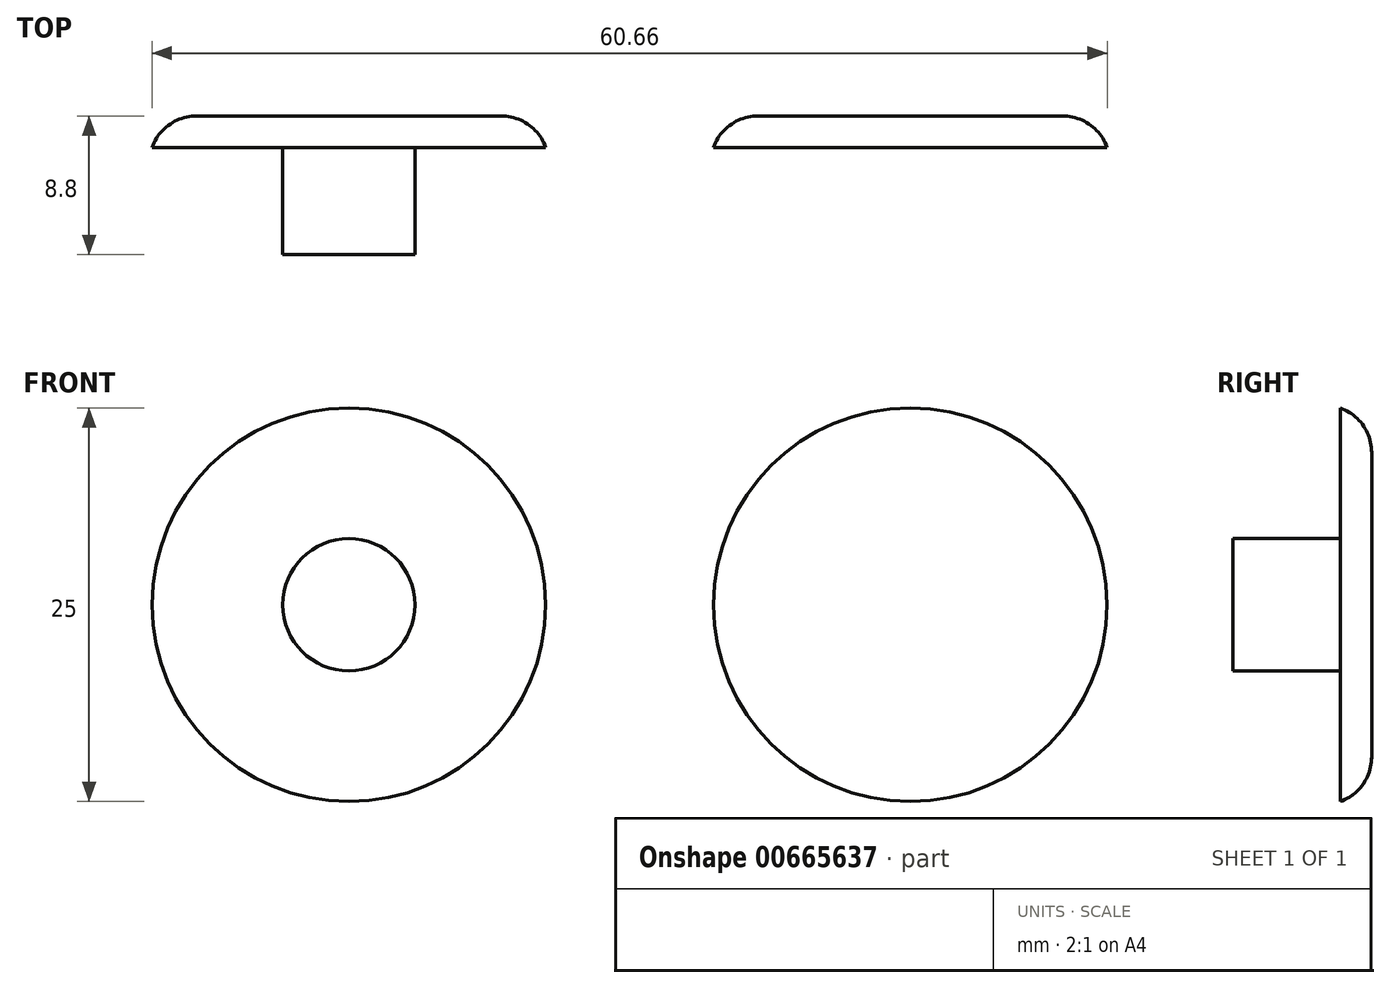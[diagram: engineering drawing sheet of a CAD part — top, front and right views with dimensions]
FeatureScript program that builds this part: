
annotation { "Feature Type Name" : "Feature", "Feature Type Description" : "" }
export const myFeature = defineFeature(function(context is Context, id is Id, definition is map)
    precondition{}
    {
        {
            var Q0;
            Q0=qCreatedBy(makeId("Front.planeOp"),FACE);
            var sketch = newSketch(context, id + "F0", { "sketchPlane" : qUnion([Q0])});
            skCircle(sketch, "E0", {"center": v(0, 0) * mm, "radius": 4.2 * mm});
            skSolve(sketch);
        }
        {
            var Q0;
            Q0=makeQuery(id+"F0.imprint","IMPRINT",FACE,{"disambiguationData":[TD([[makeQuery(id+"F0.imprint","IMPRINT",EDGE,{"derivedFrom":sQuery(id+"F0.wireOp",EDGE,"E0")}),1.0]])]});
            extrude(context, id + "F1", {"entities" : qUnion([Q0]), "depth" : 6.8 * mm, "offsetDistance" : 25 * mm});
        }
        {
            var Q0;
            Q0=makeQuery(id+"F1.opExtrude","SWEPT_BODY",BODY,{"disambiguationData":[OSD([sQuery(id+"F0.wireOp",EDGE,"E0")])]});
            transform(context, id + "F2", {"entities" : qUnion([Q0]), "transformType" : TransformType.TRANSLATION_3D, "dx" : 0 * mm, "dy" : -2 * mm, "dz" : 0 * mm, "makeCopy" : false});
        }
        {
            var Q0;
            Q0=makeQuery(id+"F1.opExtrude","CAP_FACE",FACE,{"disambiguationData":[OSD([sQuery(id+"F0.wireOp",EDGE,"E0")])],"isStart":true});
            var sketch = newSketch(context, id + "F3", { "sketchPlane" : qUnion([Q0])});
            skCircle(sketch, "E1", {"center": v(0, 0) * mm, "radius": 12.5 * mm});
            skSolve(sketch);
        }
        {
            var Q0;
            Q0=makeQuery(id+"F3.imprint","IMPRINT",FACE,{"disambiguationData":[TD([[makeQuery(id+"F3.imprint","IMPRINT",EDGE,{"derivedFrom":sQuery(id+"F3.wireOp",EDGE,"E1")}),1.0]])]});
            var Q1;
            Q1=makeQuery(id+"F3.imprint","IMPRINT",FACE,{"disambiguationData":[TD([[makeQuery(id+"F3.imprint","IMPRINT",EDGE,{"derivedFrom":makeQuery(id+"F1.opExtrude","CAP_EDGE",EDGE,{"disambiguationData":[OSD([sQuery(id+"F0.wireOp",EDGE,"E0")])],"isStart":true})}),-1.0]])]});
            extrude(context, id + "F4", {"entities" : qUnion([Q0, Q1]), "operationType" : NewBodyOperationType.ADD, "depth" : 2 * mm, "offsetDistance" : 25 * mm});
        }
        {
            var Q0;
            Q0=makeQuery(id+"F4.opExtrude","CAP_EDGE",EDGE,{"disambiguationData":[OSD([sQuery(id+"F3.wireOp",EDGE,"E1")])],"isStart":false});
            fillet(context, id + "F5", {"entities" : qUnion([Q0]), "radius" : 3 * mm, "tangentPropagation" : true, "allowEdgeOverflow" : false});
        }
        {
            var Q0;
            Q0=qCreatedBy(makeId("Front.planeOp"),FACE);
            var sketch = newSketch(context, id + "F6", { "sketchPlane" : qUnion([Q0])});
            skCircle(sketch, "E2", {"center": v(35.66, 0) * mm, "radius": 12.5 * mm});
            skSolve(sketch);
        }
        {
            var Q0;
            Q0=makeQuery(id+"F6.imprint","IMPRINT",FACE,{"disambiguationData":[TD([[makeQuery(id+"F6.imprint","IMPRINT",EDGE,{"derivedFrom":sQuery(id+"F6.wireOp",EDGE,"E2")}),1.0]])]});
            extrude(context, id + "F7", {"entities" : qUnion([Q0]), "depth" : 2 * mm, "offsetDistance" : 25 * mm});
        }
        {
            var Q0;
            Q0=makeQuery(id+"F7.opExtrude","CAP_FACE",FACE,{"disambiguationData":[OSD([sQuery(id+"F6.wireOp",EDGE,"E2")])],"isStart":true});
            fillet(context, id + "F8", {"entities" : qUnion([Q0]), "radius" : 3 * mm, "tangentPropagation" : true, "allowEdgeOverflow" : false});
        }
    });
